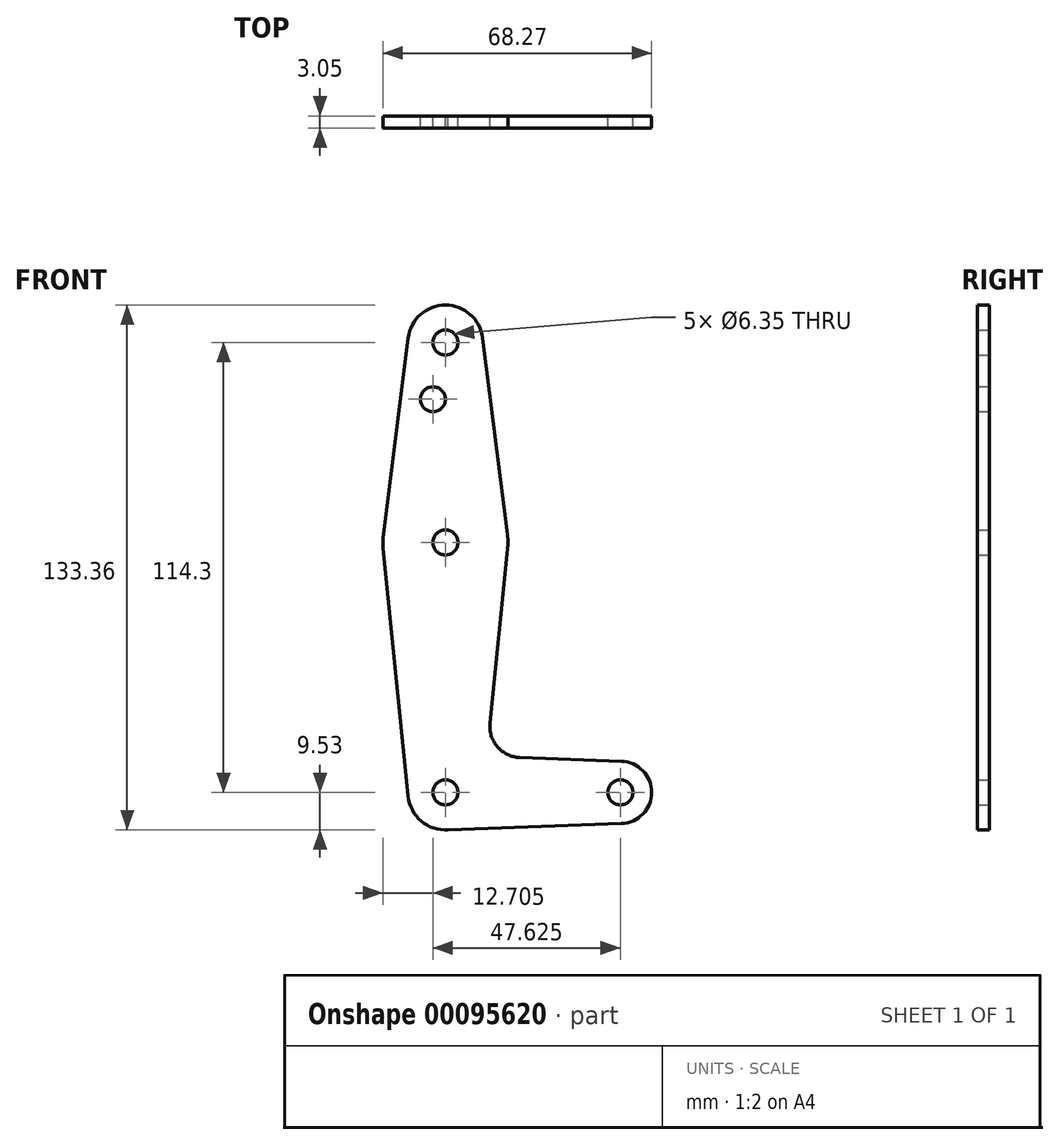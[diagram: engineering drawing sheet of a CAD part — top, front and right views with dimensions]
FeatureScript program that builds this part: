
annotation { "Feature Type Name" : "Feature", "Feature Type Description" : "" }
export const myFeature = defineFeature(function(context is Context, id is Id, definition is map)
    precondition{}
    {
        {
            var Q0;
            Q0=qCreatedBy(makeId("Front.planeOp"),FACE);
            var sketch = newSketch(context, id + "F0", { "sketchPlane" : qUnion([Q0])});
            skCircle(sketch, "E0", {"center": v(0, 114.3) * mm, "radius": 9.53 * mm});
            skCircle(sketch, "E1", {"center": v(0, 63.5) * mm, "radius": 15.88 * mm});
            skCircle(sketch, "E2", {"center": v(0, 0) * mm, "radius": 9.53 * mm});
            skCircle(sketch, "E3", {"center": v(44.45, 0) * mm, "radius": 7.94 * mm});
            skLineSegment(sketch, "E4", {"start": v(-15.8, 61.91) * mm, "end": v(-9.48, -0.95) * mm});
            skLineSegment(sketch, "E5", {"start": v(0, -9.53) * mm, "end": v(44.73, -7.93) * mm});
            skLineSegment(sketch, "E6", {"start": v(44.73, 7.93) * mm, "end": v(18.93, 8.85) * mm});
            skCircle(sketch, "E7", {"center": v(0, 114.3) * mm, "radius": 3.18 * mm});
            skCircle(sketch, "E8", {"center": v(0, 63.5) * mm, "radius": 3.18 * mm});
            skCircle(sketch, "E9", {"center": v(0, 0) * mm, "radius": 3.18 * mm});
            skCircle(sketch, "E10", {"center": v(44.45, 0) * mm, "radius": 3.18 * mm});
            skCircle(sketch, "E11", {"center": v(-3.18, 99.89) * mm, "radius": 3.18 * mm});
            skLineSegment(sketch, "E12", {"start": v(0, 55.75) * mm, "end": v(0, -9.85) * mm, "construction": true});
            skLineSegment(sketch, "E13", {"start": v(-17.45, 0) * mm, "end": v(26.89, 0) * mm, "construction": true});
            skLineSegment(sketch, "E14", {"start": v(11.3, 17.6) * mm, "end": v(15.8, 61.9) * mm});
            skLineSegment(sketch, "E15", {"start": v(-15.75, 65.48) * mm, "end": v(-9.45, 115.5) * mm});
            skLineSegment(sketch, "E16", {"start": v(9.45, 115.5) * mm, "end": v(15.75, 65.48) * mm});
            skPoint(sketch, "E17.newPointB", {"position": v(0, 9.53) * mm});
            skArc(sketch, "E17.filletArc", {"start": v(11.3, 17.6) * mm, "mid": v(13.22, 11.57) * mm, "end": v(18.93, 8.85) * mm});
            skSolve(sketch);
        }
        {
            var Q0;
            Q0 = qSketchRegion(id + "F0", true);
            extrude(context, id + "F1", {"entities" : qUnion([Q0]), "depth" : 3.05 * mm});
        }
    });
